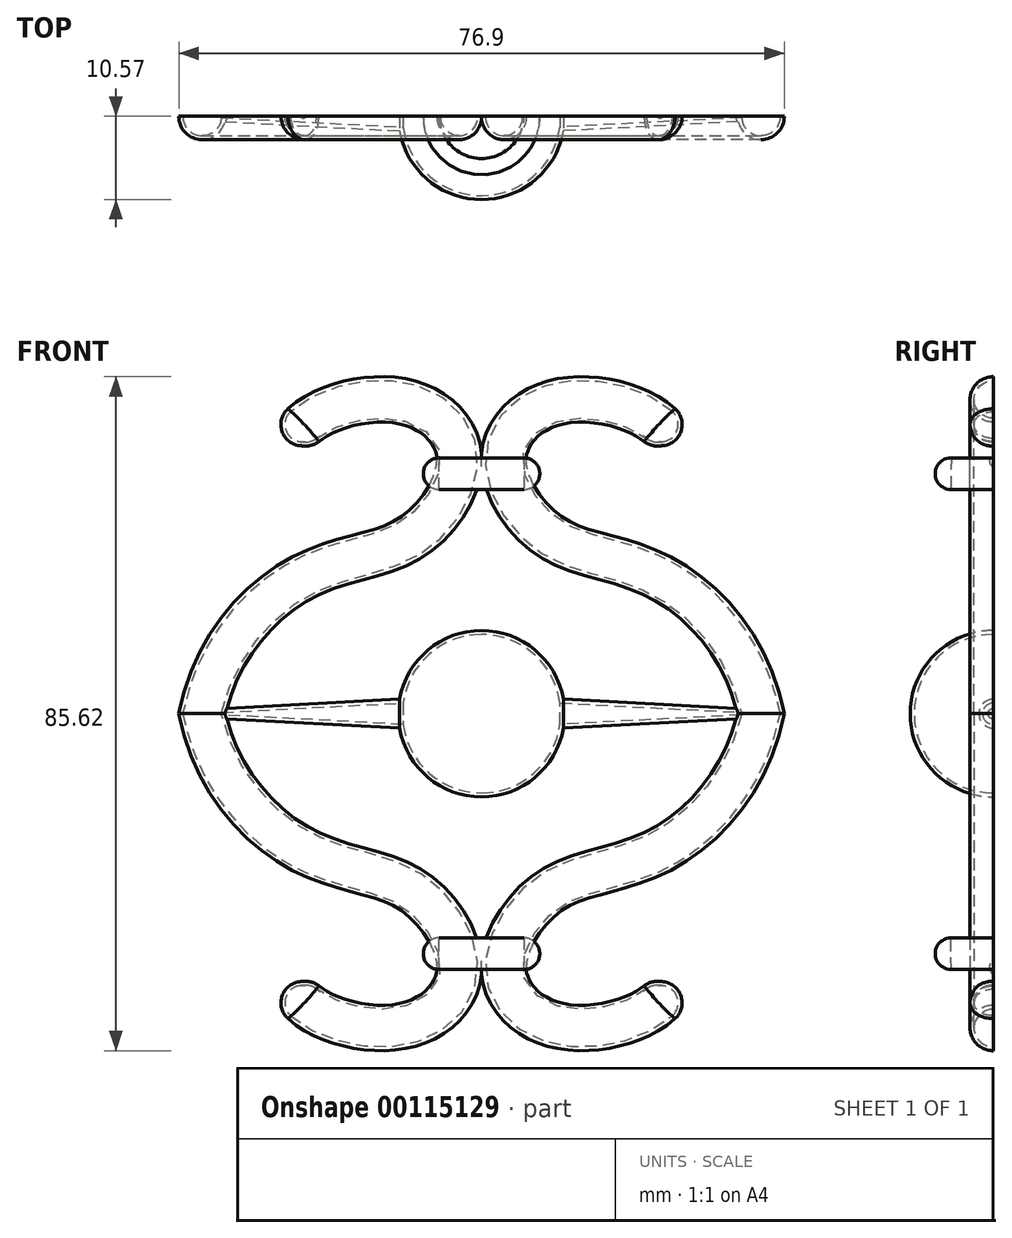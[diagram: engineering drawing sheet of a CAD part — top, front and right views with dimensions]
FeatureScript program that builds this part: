
annotation { "Feature Type Name" : "Feature", "Feature Type Description" : "" }
export const myFeature = defineFeature(function(context is Context, id is Id, definition is map)
    precondition{}
    {
        {
            var Q0;
            Q0=qCreatedBy(makeId("Front.planeOp"),FACE);
            var sketch = newSketch(context, id + "F0", { "sketchPlane" : qUnion([Q0])});
            skFitSpline(sketch, "E0", {"points": [v(34.6, 0) * mm, v(21.7, 16.86) * mm, v(8.21, 21.85) * mm, v(2.05, 33) * mm, v(10.56, 40.62) * mm, v(25.22, 34.17) * mm], "startDerivative": vector(-22.64, 103.08) * mm, "endDerivative": vector(18.93, -67.37) * mm});
            skSolve(sketch);
        }
        {
            var Q0;
            Q0=qCreatedBy(makeId("Top.planeOp"),FACE);
            var sketch = newSketch(context, id + "F1", { "sketchPlane" : qUnion([Q0])});
            skCircle(sketch, "E1", {"center": v(35.49, 0) * mm, "radius": 2.97 * mm});
            skSolve(sketch);
        }
        {
            var Q0;
            Q0=makeQuery(id+"F1.imprint","IMPRINT",FACE,{"disambiguationData":[TD([[makeQuery(id+"F1.imprint","IMPRINT",EDGE,{"derivedFrom":sQuery(id+"F1.wireOp",EDGE,"E1")}),1.0]])]});
            var Q1;
            Q1=sQuery(id+"F0.wireOp",EDGE,"E0");
            sweep(context, id + "F2", {"profiles" : qUnion([Q0]), "path" : qUnion([Q1])});
        }
        {
            var Q0;
            Q0=makeQuery(id+"F2.opSweep","SWEPT_BODY",BODY,{"disambiguationData":[OSD([sQuery(id+"F0.wireOp",EDGE,"E0"),sQuery(id+"F1.wireOp",EDGE,"E1")])]});
            var Q1;
            Q1=qCreatedBy(makeId("Top.planeOp"),FACE);
            mirror(context, id + "F3", {"operationType" : NewBodyOperationType.ADD, "entities" : qUnion([Q0]), "mirrorPlane" : qUnion([Q1])});
        }
        {
            var Q0;
            Q0=makeQuery(id+"F2.opSweep","SWEPT_BODY",BODY,{"disambiguationData":[OSD([sQuery(id+"F0.wireOp",EDGE,"E0"),sQuery(id+"F1.wireOp",EDGE,"E1")])]});
            var Q1;
            Q1=qCreatedBy(makeId("Right.planeOp"),FACE);
            mirror(context, id + "F4", {"operationType" : NewBodyOperationType.ADD, "entities" : qUnion([Q0]), "mirrorPlane" : qUnion([Q1])});
        }
        {
            var Q0;
            Q0=qCreatedBy(makeId("Front.planeOp"),FACE);
            var sketch = newSketch(context, id + "F5", { "sketchPlane" : qUnion([Q0])});
            skArc(sketch, "E2", {"start": v(0, -10.57) * mm, "mid": v(10.57, 0) * mm, "end": v(0, 10.57) * mm});
            skLineSegment(sketch, "E3", {"start": v(0, 10.57) * mm, "end": v(0, -10.57) * mm});
            skLineSegment(sketch, "E4", {"start": v(0, 19.21) * mm, "end": v(0, -20.1) * mm, "construction": true});
            skSolve(sketch);
        }
        {
            var Q0;
            Q0 = qSketchRegion(id + "F5", true);
            var Q1;
            Q1=sQuery(id+"F5.wireOp",EDGE,"E4");
            revolve(context, id + "F6", {"entities" : qUnion([Q0]), "axis" : qUnion([Q1]), "revolveType" : RevolveType.FULL});
        }
        {
            var Q0;
            Q0=qCreatedBy(makeId("Right.planeOp"),FACE);
            var sketch = newSketch(context, id + "F7", { "sketchPlane" : qUnion([Q0])});
            skCircle(sketch, "E5", {"center": v(0, 0) * mm, "radius": 2.39 * mm});
            skSolve(sketch);
        }
        {
            var Q0;
            Q0 = qSketchRegion(id + "F7", true);
            extrude(context, id + "F8", {"entities" : qUnion([Q0]), "operationType" : NewBodyOperationType.ADD, "oppositeDirection" : true, "depth" : 38.18 * mm, "hasDraft" : true, "draftAngle" : 3 * degree, "draftPullDirection" : true, "hasSecondDirection" : true, "secondDirectionOppositeDirection" : false, "secondDirectionDepth" : 38.2 * mm, "hasSecondDirectionDraft" : true, "secondDirectionDraftAngle" : 3 * degree, "secondDirectionDraftPullDirection" : true});
        }
        {
            var Q0;
            Q0=makeQuery(id+"F2.opSweep","CAP_EDGE",EDGE,{"disambiguationData":[OSD([sQuery(id+"F0.wireOp",VERTEX,"E0.end"),sQuery(id+"F1.wireOp",EDGE,"E1")])],"isStart":false});
            var Q1;
            Q1=makeQuery(id+"F4.opPattern","COPY",EDGE,{"derivedFrom":makeQuery(id+"F2.opSweep","CAP_EDGE",EDGE,{"disambiguationData":[OSD([sQuery(id+"F0.wireOp",VERTEX,"E0.end"),sQuery(id+"F1.wireOp",EDGE,"E1")])],"isStart":false}),"instanceName":"1"});
            var Q2;
            Q2=makeQuery(id+"F4.opPattern","COPY",EDGE,{"derivedFrom":makeQuery(id+"F3.opPattern","COPY",EDGE,{"derivedFrom":makeQuery(id+"F2.opSweep","CAP_EDGE",EDGE,{"disambiguationData":[OSD([sQuery(id+"F0.wireOp",VERTEX,"E0.end"),sQuery(id+"F1.wireOp",EDGE,"E1")])],"isStart":false}),"instanceName":"1"}),"instanceName":"1"});
            var Q3;
            Q3=makeQuery(id+"F3.opPattern","COPY",EDGE,{"derivedFrom":makeQuery(id+"F2.opSweep","CAP_EDGE",EDGE,{"disambiguationData":[OSD([sQuery(id+"F0.wireOp",VERTEX,"E0.end"),sQuery(id+"F1.wireOp",EDGE,"E1")])],"isStart":false}),"instanceName":"1"});
            fillet(context, id + "F9", {"entities" : qUnion([Q0, Q1, Q2, Q3]), "radius" : 2.7 * mm, "tangentPropagation" : true, "allowEdgeOverflow" : false});
        }
        {
            var Q0;
            Q0=qCreatedBy(makeId("Right.planeOp"),FACE);
            var sketch = newSketch(context, id + "F10", { "sketchPlane" : qUnion([Q0])});
            skArc(sketch, "E6", {"start": v(5.4, 28.49) * mm, "mid": v(7.4, 30.5) * mm, "end": v(5.36, 32.49) * mm});
            skLineSegment(sketch, "E7", {"start": v(5.36, 32.49) * mm, "end": v(5.4, 28.49) * mm});
            skLineSegment(sketch, "E8", {"start": v(0, 47.66) * mm, "end": v(0, -52.35) * mm, "construction": true});
            skSolve(sketch);
        }
        {
            var Q0;
            Q0 = qSketchRegion(id + "F10", true);
            var Q1;
            Q1=sQuery(id+"F10.wireOp",EDGE,"E8");
            revolve(context, id + "F11", {"entities" : qUnion([Q0]), "axis" : qUnion([Q1]), "revolveType" : RevolveType.FULL});
        }
        {
            var Q0;
            Q0=makeQuery(id+"F11.opRevolve","SWEPT_BODY",BODY,{"disambiguationData":[OSD([sQuery(id+"F10.wireOp",EDGE,"E6"),sQuery(id+"F10.wireOp",EDGE,"E7")])]});
            var Q1;
            Q1=qCreatedBy(makeId("Top.planeOp"),FACE);
            mirror(context, id + "F12", {"entities" : qUnion([Q0]), "mirrorPlane" : qUnion([Q1])});
        }
        {
            var Q0;
            Q0=qCreatedBy(makeId("Right.planeOp"),FACE);
            var sketch = newSketch(context, id + "F13", { "sketchPlane" : qUnion([Q0])});
            skLineSegment(sketch, "E9", {"start": v(0, 51.18) * mm, "end": v(0, -48.54) * mm});
            skLineSegment(sketch, "E10", {"start": v(0, -48.54) * mm, "end": v(13.2, -48.54) * mm});
            skLineSegment(sketch, "E11", {"start": v(13.2, -48.54) * mm, "end": v(13.2, 51.18) * mm});
            skLineSegment(sketch, "E12", {"start": v(13.2, 51.18) * mm, "end": v(0, 51.18) * mm});
            skSolve(sketch);
        }
        {
            var Q0;
            Q0 = qSketchRegion(id + "F13", true);
            extrude(context, id + "F14", {"entities" : qUnion([Q0]), "operationType" : NewBodyOperationType.REMOVE, "endBound" : BoundingType.THROUGH_ALL, "depth" : 25 * mm, "hasSecondDirection" : true, "secondDirectionBound" : SecondDirectionBoundingType.THROUGH_ALL, "secondDirectionOppositeDirection" : true, "secondDirectionDepth" : 25 * mm});
        }
        {
            var Q0;
            {var subQ0=sQuery(id+"F1.wireOp",EDGE,"E1");var subQ1=makeQuery(id+"F2.opSweep","SWEPT_FACE",FACE,{"disambiguationData":[OSD([sQuery(id+"F0.wireOp",EDGE,"E0"),subQ0])]});var subQ2=makeQuery(id+"F3.opPattern","COPY",FACE,{"derivedFrom":subQ1,"instanceName":"1"});var subQ3=sQuery(id+"F0.wireOp",VERTEX,"E0.end");var subQ4=makeQuery(id+"F2.opSweep","CAP_FACE",FACE,{"disambiguationData":[OSD([subQ3,subQ0])],"isStart":false});var subQ5=makeQuery(id+"F3.opPattern","COPY",FACE,{"derivedFrom":subQ4,"instanceName":"1"});var subQ6=makeQuery(id+"F2.opSweep","CAP_EDGE",EDGE,{"disambiguationData":[OSD([subQ3,subQ0])],"isStart":false});var subQ7=makeQuery(id+"F3.opPattern","COPY",EDGE,{"derivedFrom":subQ6,"instanceName":"1"});Q0=makeQuery(id+"F14.boolean.opBoolean","COPY",FACE,{"disambiguationData":[TD([subQ4,subQ1,subQ5,subQ2,makeQuery(id+"F4.opPattern","COPY",FACE,{"derivedFrom":subQ4,"instanceName":"1"}),makeQuery(id+"F4.opPattern","COPY",FACE,{"derivedFrom":subQ1,"instanceName":"1"}),makeQuery(id+"F4.opPattern","COPY",FACE,{"derivedFrom":subQ5,"instanceName":"1"}),makeQuery(id+"F4.opPattern","COPY",FACE,{"derivedFrom":subQ2,"instanceName":"1"}),makeQuery(id+"F6.opRevolve","SWEPT_FACE",FACE,{"disambiguationData":[OSD([sQuery(id+"F5.wireOp",EDGE,"E2")])]}),makeQuery(id+"F8.opExtrude","SWEPT_FACE",FACE,{"disambiguationData":[OSD([sQuery(id+"F7.wireOp",EDGE,"E5")])]}),makeQuery(id+"F9.opFillet","BLEND_FACE",FACE,{"disambiguationData":[OSD([subQ3,subQ0]),TDD([subQ6])]}),makeQuery(id+"F9.opFillet","BLEND_FACE",FACE,{"disambiguationData":[OSD([subQ3,subQ0]),TDD([subQ7])]}),makeQuery(id+"F9.opFillet","BLEND_FACE",FACE,{"disambiguationData":[OSD([subQ3,subQ0]),TDD([makeQuery(id+"F4.opPattern","COPY",EDGE,{"derivedFrom":subQ6,"instanceName":"1"})])]}),makeQuery(id+"F9.opFillet","BLEND_FACE",FACE,{"disambiguationData":[OSD([subQ3,subQ0]),TDD([makeQuery(id+"F4.opPattern","COPY",EDGE,{"derivedFrom":subQ7,"instanceName":"1"})])]})])],"derivedFrom":makeQuery(id+"F14.opExtrude","SWEPT_FACE",FACE,{"disambiguationData":[OSD([sQuery(id+"F13.wireOp",EDGE,"E9")])]})});}
            shell(context, id + "F15", {"entities" : qUnion([Q0]), "thickness" : .5 * mm});
        }
    });
